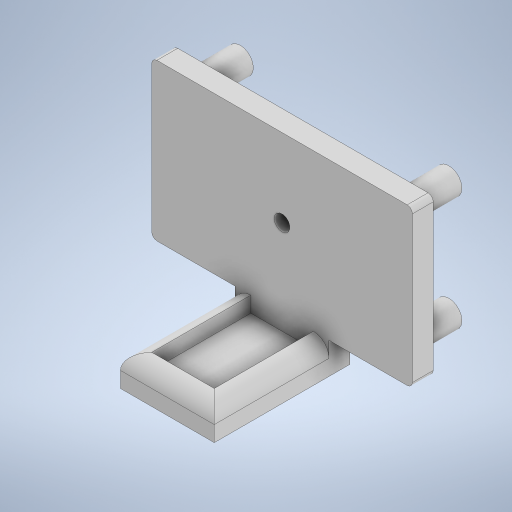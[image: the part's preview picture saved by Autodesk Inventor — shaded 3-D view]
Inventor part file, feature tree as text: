
AUTODESK INVENTOR PART (.ipt)
format: ipt  version: 2023 (Build 270158000, 158)  size: 302,592 bytes
history: native  units: in
note: dims shown in document units (in); Inventor stores cm internally (conversion verified against a paired STEP export)
features: sketch x7, extrude x4, fillet x3, hole x1
ambient origin geometry x8: Origin, YZ Plane, XZ Plane, XY Plane, X Axis, Y Axis, Z Axis, Center Point
bodies: Solid1 (feature_tree)
feature tree (15):
  extrude  "Extrusion1"  Depth=1.1811in
  fillet  "Fillet1"  Radius=0.1575in
  fillet  "Fillet2"  Radius=0.0394in
  hole  "Hole2"  [1 undecoded]
  sketch  "Sketch6"  dims[d20=0.1181in d21=0.2362in d22=0.1575in d23=0.0787in d24=90.0deg d25=0.315in d26=0.8108in d27=0.1969in]
  sketch  "Sketch18"  dims[d28=0.1969in d29=0.1969in]
  extrude  "Extrusion10"  Depth=0.315in
  extrude  "Extrusion11"  Depth=0.1969in
  sketch  "Sketch20"  dims[d40=0.1969in]
  extrude  "Extrusion12"  Depth=0.1969in
  fillet  "Fillet11"  Radius=0.1969in
  sketch  "Sketch1"  dims[d0=1.9685in d1=1.1811in d2=0.1575in d3=0.0in d4=0.0394in]
  sketch  "Sketch4"  dims[d5=0.0394in d19=0.1181in]
  sketch  "Sketch19"  dims[d30=0.1969in d38=0.1969in d39=0.1969in]
  sketch  "Sketch21"  dims[d41=0.1969in d42=0.1575in d43=0.1575in d44=0.1575in d45=0.1575in d82=0.4724in d83=0.0in d84=0.7087in d85=0.2362in d86=1.0236in d87=0.0in d88=0.4724in d89=0.748in d90=0.1181in d91=0.0in d92=0.1181in d7=0.0394in d8=0.0394in d9=0.0394in d10=0.0059in d11=0.0098in d12=0.0148in d13=0.5635in d14=0.0295in d15=0.8108in d16=0.0025in d17=0.0295in d18=0.0148in d31=0.0394in d32=0.0394in d33=0.0394in d34=0.0059in d35=0.0098in d36=0.0148in d37=0.5635in d73=0.0in d74=0.0in d75=0.0in d76=0.0in d77=0.0344in d78=0.0197in d79=0.0344in d93=0.0148in d94=0.0in d95=0.0in]
note: 1 required parameter value undecoded (feature->parameter linkage not recoverable at this tier; creation-order binding heuristic only, values carry confidence <= 0.55)
